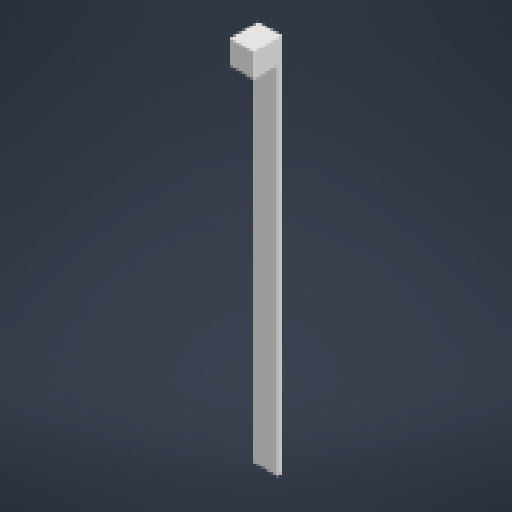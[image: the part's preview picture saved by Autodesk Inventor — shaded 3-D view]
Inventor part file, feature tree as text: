
AUTODESK INVENTOR PART (.ipt)
format: ipt  version: 2024 (Build 280153000, 153)  size: 128,512 bytes
history: native  units: mm
features: extrude x2, sketch x2, other x1
ambient origin geometry x8: Origin, YZ Plane, XZ Plane, XY Plane, X Axis, Y Axis, Z Axis, Center Point
bodies: Body1 (feature_tree)
feature tree (5):
  other  "솔리드1"
  extrude  "돌출1"  Depth=5.0mm
  extrude  "돌출2"  Depth=80.0mm
  sketch  "스케치1"
  sketch  "스케치2"
